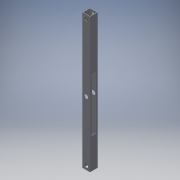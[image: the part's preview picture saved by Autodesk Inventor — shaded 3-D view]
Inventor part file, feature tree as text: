
AUTODESK INVENTOR PART (.ipt)
format: ipt  version: 2016 (Build 200138000, 138)  size: 138,752 bytes
history: native  units: in
note: dims shown in document units (in); Inventor stores cm internally (conversion verified against a paired STEP export)
features: extrude x5, sketch x5
ambient origin geometry x8: Origin, YZ Plane, XZ Plane, XY Plane, X Axis, Y Axis, Z Axis, Center Point
bodies: Solid1 (feature_tree)
feature tree (10):
  extrude  "Extrusion1"  Depth=1.0in
  extrude  "Extrusion2"  Depth=17.5in TaperAngle=0.0deg
  extrude  "Extrusion4"  Depth=0.5in
  extrude  "Extrusion5"  Depth=1.0in
  extrude  "Extrusion6"  Depth=3.5in
  sketch  "Sketch1"  dims[d0=1.0in d1=1.0in]
  sketch  "Sketch2"  dims[d2=0.0625in d3=17.5in d4=0.0in]
  sketch  "Sketch4"  dims[d5=0.5in d6=0.5in]
  sketch  "Sketch5"  dims[d7=1.0in d8=0.0in d17=0.5in]
  sketch  "Sketch6"  dims[d18=0.5in d19=0.5in d20=1.0in d21=0.0in d22=0.5in d23=0.5in d24=9.25in d25=1.0in d26=0.0in d28=0.2in d29=0.2in d30=6.945in d31=1.0in d32=0.0in d33=3.5in]
